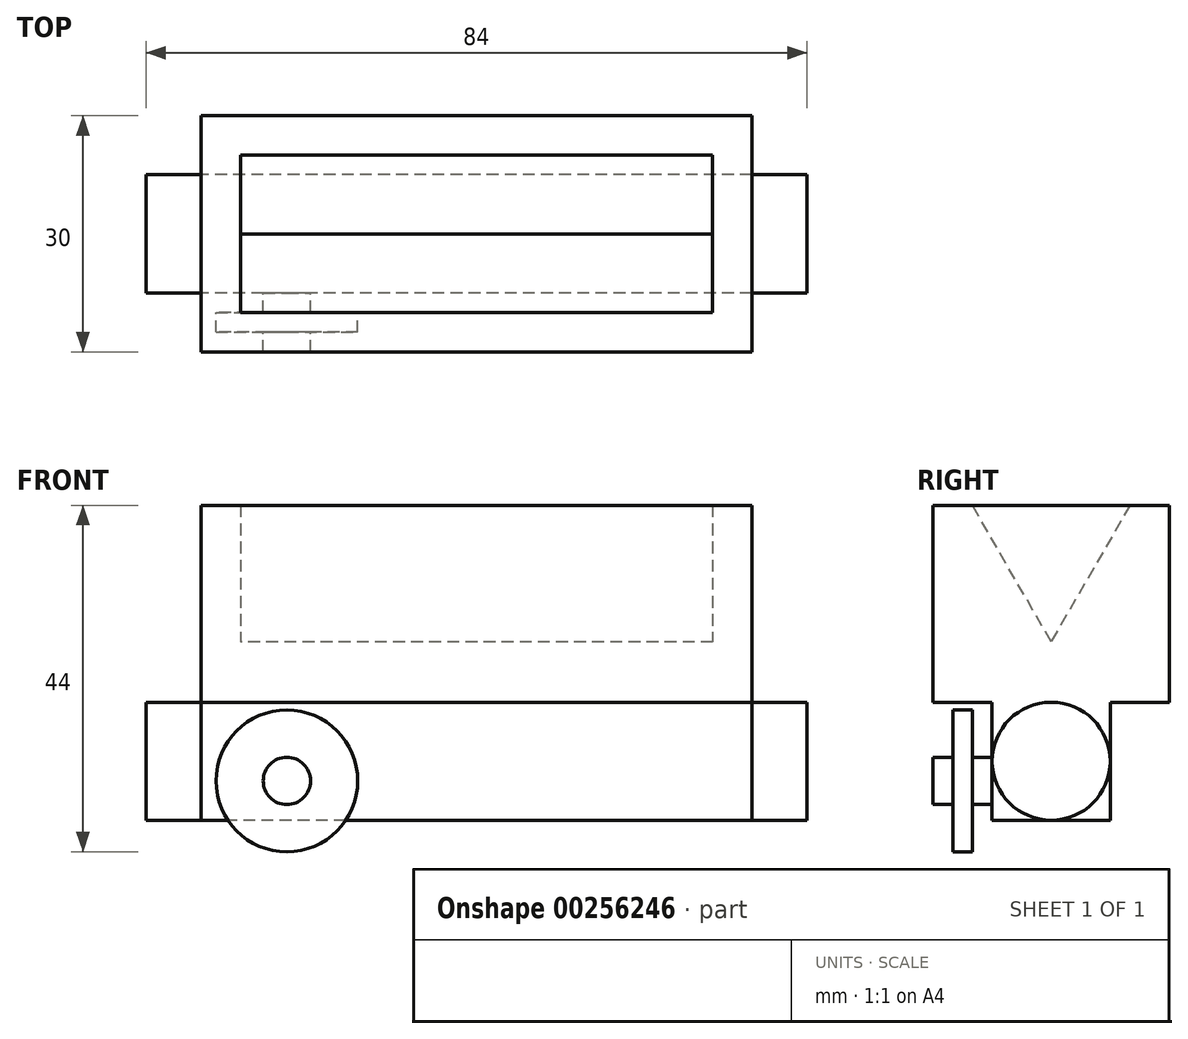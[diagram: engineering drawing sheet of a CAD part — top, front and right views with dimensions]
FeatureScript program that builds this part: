
annotation { "Feature Type Name" : "Feature", "Feature Type Description" : "" }
export const myFeature = defineFeature(function(context is Context, id is Id, definition is map)
    precondition{}
    {
        {
            var Q0;
            Q0=qCreatedBy(makeId("Front.planeOp"),FACE);
            var sketch = newSketch(context, id + "F0", { "sketchPlane" : qUnion([Q0])});
            skLineSegment(sketch, "E0.bottom", {"start": v(35, 12.5) * mm, "end": v(-35, 12.5) * mm});
            skLineSegment(sketch, "E0.top", {"start": v(35, -12.5) * mm, "end": v(-35, -12.5) * mm});
            skLineSegment(sketch, "E0.left", {"start": v(35, 12.5) * mm, "end": v(35, -12.5) * mm});
            skLineSegment(sketch, "E0.right", {"start": v(-35, 12.5) * mm, "end": v(-35, -12.5) * mm});
            skPoint(sketch, "E0.middle", {"position": v(0, 0) * mm});
            skSolve(sketch);
        }
        {
            var Q0;
            Q0 = qSketchRegion(id + "F0", true);
            extrude(context, id + "F1", {"entities" : qUnion([Q0]), "endBound" : BoundingType.SYMMETRIC, "depth" : 30 * mm});
        }
        {
            var Q0;
            Q0=makeQuery(id+"F1.opExtrude","SWEPT_FACE",FACE,{"disambiguationData":[OSD([sQuery(id+"F0.wireOp",EDGE,"E0.top")])]});
            var sketch = newSketch(context, id + "F2", { "sketchPlane" : qUnion([Q0])});
            skLineSegment(sketch, "E1.bottom", {"start": v(35, 7.5) * mm, "end": v(-35, 7.5) * mm});
            skLineSegment(sketch, "E1.top", {"start": v(35, -7.5) * mm, "end": v(-35, -7.5) * mm});
            skLineSegment(sketch, "E1.left", {"start": v(35, 7.5) * mm, "end": v(35, -7.5) * mm});
            skLineSegment(sketch, "E1.right", {"start": v(-35, 7.5) * mm, "end": v(-35, -7.5) * mm});
            skPoint(sketch, "E1.middle", {"position": v(0, 0) * mm});
            skSolve(sketch);
        }
        {
            var Q0;
            Q0 = qSketchRegion(id + "F2", true);
            extrude(context, id + "F3", {"entities" : qUnion([Q0]), "operationType" : NewBodyOperationType.ADD, "depth" : 15 * mm});
        }
        {
            var Q0;
            Q0=makeQuery(id+"F3.boolean.opBoolean","MERGE",FACE,{"derivedFrom":[makeQuery(id+"F1.opExtrude","SWEPT_FACE",FACE,{"disambiguationData":[OSD([sQuery(id+"F0.wireOp",EDGE,"E0.left")])]}),makeQuery(id+"F3.opExtrude","SWEPT_FACE",FACE,{"disambiguationData":[OSD([sQuery(id+"F2.wireOp",EDGE,"E1.left")])]})]});
            var sketch = newSketch(context, id + "F4", { "sketchPlane" : qUnion([Q0])});
            skPoint(sketch, "E2", {"position": v(0, -20) * mm});
            skPoint(sketch, "E2.positionSnap0", {"position": v(7.5, -20) * mm});
            skPoint(sketch, "E3", {"position": v(-7.5, -20) * mm});
            skCircle(sketch, "E4", {"center": v(0, -20) * mm, "radius": 7.5 * mm});
            skSolve(sketch);
        }
        {
            var Q0;
            {var subQ0=sQuery(id+"F4.wireOp",EDGE,"E4");var subQ1=sQuery(id+"F2.wireOp",EDGE,"E1.left");var subQ6=makeQuery(id+"F4.imprint","INTERSECT",VERTEX,{"derivedFrom":[makeQuery(id+"F3.opExtrude","CAP_EDGE",EDGE,{"disambiguationData":[OSD([subQ1])],"isStart":false}),subQ0]});Q0=makeQuery(id+"F4.imprint","IMPRINT",FACE,{"disambiguationData":[TD([[makeQuery(id+"F4.imprint","IMPRINT",EDGE,{"disambiguationData":[TD([[subQ6,1.0]])],"derivedFrom":subQ0}),1.0]])]});}
            extrude(context, id + "F5", {"entities" : qUnion([Q0]), "operationType" : NewBodyOperationType.ADD, "depth" : 7 * mm});
        }
        {
            var Q0;
            Q0=makeQuery(id+"F3.boolean.opBoolean","MERGE",FACE,{"derivedFrom":[makeQuery(id+"F1.opExtrude","SWEPT_FACE",FACE,{"disambiguationData":[OSD([sQuery(id+"F0.wireOp",EDGE,"E0.right")])]}),makeQuery(id+"F3.opExtrude","SWEPT_FACE",FACE,{"disambiguationData":[OSD([sQuery(id+"F2.wireOp",EDGE,"E1.right")])]})]});
            var sketch = newSketch(context, id + "F6", { "sketchPlane" : qUnion([Q0])});
            skPoint(sketch, "E5", {"position": v(0, -20) * mm});
            skPoint(sketch, "E5.positionSnap0", {"position": v(-7.5, -20) * mm});
            skPoint(sketch, "E6", {"position": v(7.5, -20) * mm});
            skPoint(sketch, "E7", {"position": v(0, -27.5) * mm});
            skPoint(sketch, "E8", {"position": v(0, -12.5) * mm});
            skCircle(sketch, "E9", {"center": v(0, -20) * mm, "radius": 7.5 * mm});
            skSolve(sketch);
        }
        {
            var Q0;
            Q0 = qSketchRegion(id + "F6", true);
            extrude(context, id + "F7", {"entities" : qUnion([Q0]), "operationType" : NewBodyOperationType.ADD, "depth" : 7 * mm});
        }
        {
            var Q0;
            Q0=makeQuery(id+"F1.opExtrude","SWEPT_FACE",FACE,{"disambiguationData":[OSD([sQuery(id+"F0.wireOp",EDGE,"E0.bottom")])]});
            var sketch = newSketch(context, id + "F8", { "sketchPlane" : qUnion([Q0])});
            skLineSegment(sketch, "E10.bottom", {"start": v(30, 10) * mm, "end": v(-30, 10) * mm});
            skLineSegment(sketch, "E10.top", {"start": v(30, -10) * mm, "end": v(-30, -10) * mm});
            skLineSegment(sketch, "E10.left", {"start": v(30, 10) * mm, "end": v(30, -10) * mm});
            skLineSegment(sketch, "E10.right", {"start": v(-30, 10) * mm, "end": v(-30, -10) * mm});
            skPoint(sketch, "E10.middle", {"position": v(0, 0) * mm});
            skSolve(sketch);
        }
        {
            var Q0;
            Q0=qCreatedBy(makeId("Right.planeOp"),FACE);
            var sketch = newSketch(context, id + "F9", { "sketchPlane" : qUnion([Q0])});
            skLineSegment(sketch, "E11", {"start": v(10, 12.5) * mm, "end": v(0, -4.82) * mm});
            skPoint(sketch, "E11.endSnap0", {"position": v(0, 12.5) * mm});
            skLineSegment(sketch, "E12", {"start": v(0, -4.82) * mm, "end": v(-10, 12.5) * mm});
            skLineSegment(sketch, "E13", {"start": v(-10, 12.5) * mm, "end": v(10, 12.5) * mm});
            skSolve(sketch);
        }
        {
            var Q0;
            Q0 = qSketchRegion(id + "F9", true);
            extrude(context, id + "F10", {"entities" : qUnion([Q0]), "operationType" : NewBodyOperationType.REMOVE, "depth" : 30 * mm});
        }
        {
            var Q0;
            Q0 = qSketchRegion(id + "F9", true);
            extrude(context, id + "F11", {"entities" : qUnion([Q0]), "operationType" : NewBodyOperationType.REMOVE, "oppositeDirection" : true, "depth" : 30 * mm});
        }
        {
            var Q0;
            Q0=makeQuery(id+"F3.opExtrude","SWEPT_FACE",FACE,{"disambiguationData":[OSD([sQuery(id+"F2.wireOp",EDGE,"E1.bottom")])]});
            var sketch = newSketch(context, id + "F12", { "sketchPlane" : qUnion([Q0])});
            skCircle(sketch, "E14", {"center": v(-24.1, -22.5) * mm, "radius": 3 * mm});
            skSolve(sketch);
        }
        {
            var Q0;
            Q0=makeQuery(id+"F12.imprint","IMPRINT",FACE,{"disambiguationData":[TD([[makeQuery(id+"F12.imprint","IMPRINT",EDGE,{"derivedFrom":sQuery(id+"F12.wireOp",EDGE,"E14")}),1.0]])]});
            var Q1;
            Q1=sQuery(id+"F12.wireOp",EDGE,"E14");
            extrude(context, id + "F13", {"entities" : qUnion([Q0]), "operationType" : NewBodyOperationType.ADD, "surfaceEntities" : qUnion([Q1]), "depth" : 2.5 * mm});
        }
        {
            var Q0;
            Q0=makeQuery(id+"F13.opExtrude","CAP_FACE",FACE,{"disambiguationData":[OSD([sQuery(id+"F12.wireOp",EDGE,"E14")])],"isStart":false});
            var sketch = newSketch(context, id + "F14", { "sketchPlane" : qUnion([Q0])});
            skPoint(sketch, "E15", {"position": v(-24.1, -22.5) * mm});
            skPoint(sketch, "E16", {"position": v(-35, -22.5) * mm});
            skPoint(sketch, "E17", {"position": v(-33.1, -22.5) * mm});
            skLineSegment(sketch, "E18", {"start": v(-33.1, -22.5) * mm, "end": v(-24.1, -22.5) * mm});
            skSolve(sketch);
        }
        {
            var Q0;
            Q0 = qSketchRegion(id + "F14", true);
            var Q1;
            Q1=sQuery(id+"F14.wireOp",EDGE,"E18");
            extrude(context, id + "F15", {"entities" : qUnion([Q0]), "bodyType" : ToolBodyType.SURFACE, "operationType" : NewBodyOperationType.ADD, "surfaceEntities" : qUnion([Q1]), "depth" : 2.5 * mm});
        }
        {
            var Q0;
            Q0=makeQuery(id+"F15.opExtrude","SWEPT_FACE",FACE,{"disambiguationData":[OSD([sQuery(id+"F14.wireOp",EDGE,"E18")])]});
            var Q1;
            Q1=makeQuery(id+"F15.opExtrude","SWEPT_EDGE",EDGE,{"disambiguationData":[OSD([sQuery(id+"F14.wireOp",VERTEX,"E18.end")])]});
            revolve(context, id + "F16", {"operationType" : NewBodyOperationType.ADD, "entities" : qUnion([Q0]), "axis" : qUnion([Q1]), "revolveType" : RevolveType.FULL});
        }
        {
            var Q0;
            {var subQ0=sQuery(id+"F14.wireOp",EDGE,"E18");Q0=makeQuery(id+"F16.opRevolve","SWEPT_FACE",FACE,{"disambiguationData":[OSD([subQ0]),TDD([makeQuery(id+"F15.opExtrude","CAP_EDGE",EDGE,{"disambiguationData":[OSD([subQ0])],"isStart":false})])]});}
            var sketch = newSketch(context, id + "F17", { "sketchPlane" : qUnion([Q0])});
            skCircle(sketch, "E19", {"center": v(-24.1, -22.5) * mm, "radius": 3 * mm});
            skSolve(sketch);
        }
        {
            var Q0;
            Q0=makeQuery(id+"F17.imprint","IMPRINT",FACE,{"disambiguationData":[TD([[makeQuery(id+"F17.imprint","IMPRINT",EDGE,{"derivedFrom":sQuery(id+"F17.wireOp",EDGE,"E19")}),1.0]])]});
            extrude(context, id + "F18", {"entities" : qUnion([Q0]), "operationType" : NewBodyOperationType.ADD, "depth" : 2.5 * mm});
        }
    });
